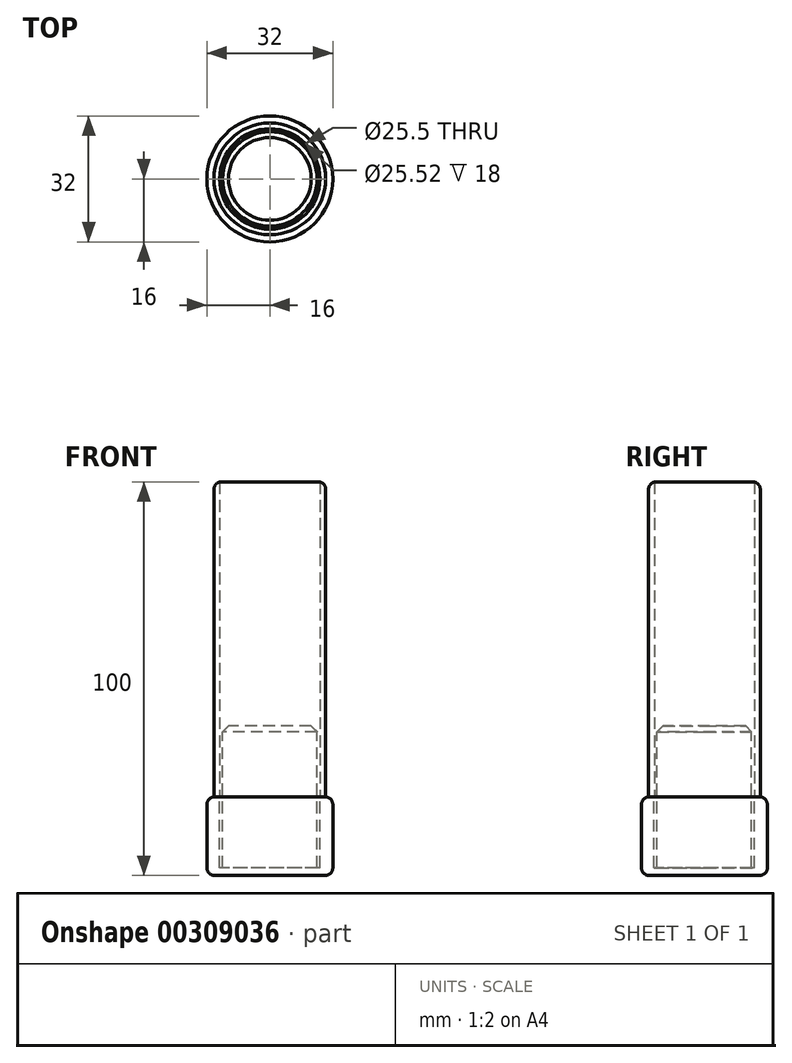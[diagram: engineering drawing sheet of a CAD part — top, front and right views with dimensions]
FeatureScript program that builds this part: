
annotation { "Feature Type Name" : "Feature", "Feature Type Description" : "" }
export const myFeature = defineFeature(function(context is Context, id is Id, definition is map)
    precondition{}
    {
        {
            var Q0;
            Q0=qCreatedBy(makeId("Top.planeOp"),FACE);
            var sketch = newSketch(context, id + "F0", { "sketchPlane" : qUnion([Q0])});
            skCircle(sketch, "E0", {"center": v(0, 0) * mm, "radius": 16 * mm});
            skSolve(sketch);
        }
        {
            var Q0;
            Q0 = qSketchRegion(id + "F0", true);
            extrude(context, id + "F1", {"entities" : qUnion([Q0]), "depth" : 20 * mm});
        }
        {
            var Q0;
            Q0=makeQuery(id+"F1.opExtrude","CAP_FACE",FACE,{"disambiguationData":[OSD([sQuery(id+"F0.wireOp",EDGE,"E0")])],"isStart":false});
            cPlane(context, id + "F2", {"entities" : qUnion([Q0]), "cplaneType" : CPlaneType.OFFSET, "offset" : 0 * mm, "width" : 150 * mm, "height" : 150 * mm});
        }
        {
            var Q0;
            Q0=qCreatedBy(id+"F2.planeOp",FACE);
            var sketch = newSketch(context, id + "F3", { "sketchPlane" : qUnion([Q0])});
            skCircle(sketch, "E1", {"center": v(0, 0) * mm, "radius": 14.2 * mm});
            skCircle(sketch, "E2", {"center": v(0, 0) * mm, "radius": 12.75 * mm});
            skSolve(sketch);
        }
        {
            var Q0;
            Q0=makeQuery(id+"F3.imprint","IMPRINT",FACE,{"disambiguationData":[TD([[makeQuery(id+"F3.imprint","IMPRINT",EDGE,{"derivedFrom":sQuery(id+"F3.wireOp",EDGE,"E1")}),1.0]])]});
            extrude(context, id + "F4", {"entities" : qUnion([Q0]), "operationType" : NewBodyOperationType.ADD, "depth" : 80 * mm});
        }
        {
            var Q0;
            Q0=qCreatedBy(id+"F2.planeOp",FACE);
            var sketch = newSketch(context, id + "F5", { "sketchPlane" : qUnion([Q0])});
            skCircle(sketch, "E3", {"center": v(0, 0) * mm, "radius": 12 * mm});
            skCircle(sketch, "E4", {"center": v(0, 0) * mm, "radius": 12.76 * mm});
            skSolve(sketch);
        }
        {
            var Q0;
            Q0=makeQuery(id+"F5.imprint","IMPRINT",FACE,{"disambiguationData":[TD([[makeQuery(id+"F5.imprint","IMPRINT",EDGE,{"derivedFrom":sQuery(id+"F5.wireOp",EDGE,"E3")}),-1.0]])]});
            extrude(context, id + "F6", {"entities" : qUnion([Q0]), "operationType" : NewBodyOperationType.REMOVE, "oppositeDirection" : true, "depth" : 18 * mm});
        }
        {
            var Q0;
            Q0=makeQuery(id+"F4.boolean.opBoolean","SPLIT",FACE,{"disambiguationData":[TD([makeQuery(id+"F4.opExtrude","SWEPT_FACE",FACE,{"disambiguationData":[OSD([sQuery(id+"F3.wireOp",EDGE,"E2")])]})])],"derivedFrom":makeQuery(id+"F1.opExtrude","CAP_FACE",FACE,{"disambiguationData":[OSD([sQuery(id+"F0.wireOp",EDGE,"E0")])],"isStart":false})});
            extrude(context, id + "F7", {"entities" : qUnion([Q0]), "operationType" : NewBodyOperationType.ADD, "depth" : 18 * mm});
        }
        {
            var Q0;
            Q0=makeQuery(id+"F1.opExtrude","CAP_EDGE",EDGE,{"disambiguationData":[OSD([sQuery(id+"F0.wireOp",EDGE,"E0")])],"isStart":false});
            var Q1;
            Q1=makeQuery(id+"F1.opExtrude","CAP_EDGE",EDGE,{"disambiguationData":[OSD([sQuery(id+"F0.wireOp",EDGE,"E0")])],"isStart":true});
            var Q2;
            Q2=makeQuery(id+"F4.opExtrude","CAP_EDGE",EDGE,{"disambiguationData":[OSD([sQuery(id+"F3.wireOp",EDGE,"E1")])],"isStart":false});
            fillet(context, id + "F8", {"entities" : qUnion([Q0, Q1, Q2]), "radius" : 2 * mm, "tangentPropagation" : true, "allowEdgeOverflow" : false});
        }
        {
            var Q0;
            Q0=makeQuery(id+"F7.opExtrude","CAP_FACE",FACE,{"disambiguationData":[OSD([sQuery(id+"F0.wireOp",EDGE,"E0")])],"isStart":false});
            chamfer(context, id + "F9", {"entities" : qUnion([Q0]), "width" : 1.5 * mm, "tangentPropagation" : true});
        }
    });
